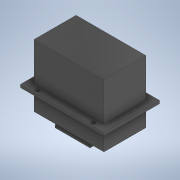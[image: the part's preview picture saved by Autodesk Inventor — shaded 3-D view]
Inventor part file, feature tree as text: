
AUTODESK INVENTOR PART (.ipt)
format: ipt  version: 2022 (Build 260153000, 153)  size: 184,320 bytes
history: native  units: in
note: dims shown in document units (in); Inventor stores cm internally (conversion verified against a paired STEP export)
features: extrude x8, sketch x8
ambient origin geometry x8: Origin, YZ Plane, XZ Plane, XY Plane, X Axis, Y Axis, Z Axis, Center Point
bodies: Solid1 (feature_tree)
feature tree (16):
  extrude  "Extrusion1"  Depth=1.1811in
  extrude  "Extrusion2"  Depth=2.3622in
  extrude  "Extrusion3"  Depth=1.1811in TaperAngle=0.0deg
  extrude  "Extrusion4"  Depth=1.1811in
  extrude  "Extrusion5"  Depth=0.1969in TaperAngle=0.0deg
  extrude  "Extrusion6"  Depth=0.1181in TaperAngle=0.0deg
  extrude  "Extrusion7"  Depth=0.9843in
  extrude  "Extrusion8"  Depth=0.1181in
  sketch  "Sketch1"  dims[d0=1.9685in d1=1.1811in]
  sketch  "Sketch2"  dims[d2=1.9685in d3=0.0in d4=2.3622in]
  sketch  "Sketch3"  dims[d5=1.5748in d6=1.1811in d7=0.0in]
  sketch  "Sketch4"  dims[d8=1.9685in d9=1.1811in]
  sketch  "Sketch5"  dims[d10=1.1024in d11=0.0in d12=0.1969in d13=0.0in]
  sketch  "Sketch6"  dims[d14=0.1969in d15=0.1181in d16=0.0in]
  sketch  "Sketch7"  dims[d19=0.9843in d20=0.9843in]
  sketch  "Sketch8"  dims[d21=0.1181in d22=0.1181in d23=0.1181in d24=0.1181in d25=0.0787in d26=0.0in d27=0.1969in d28=0.1181in d29=0.0in d38=0.1181in d39=0.1181in d40=0.1181in d41=0.1181in d42=0.1181in d43=0.0in]
